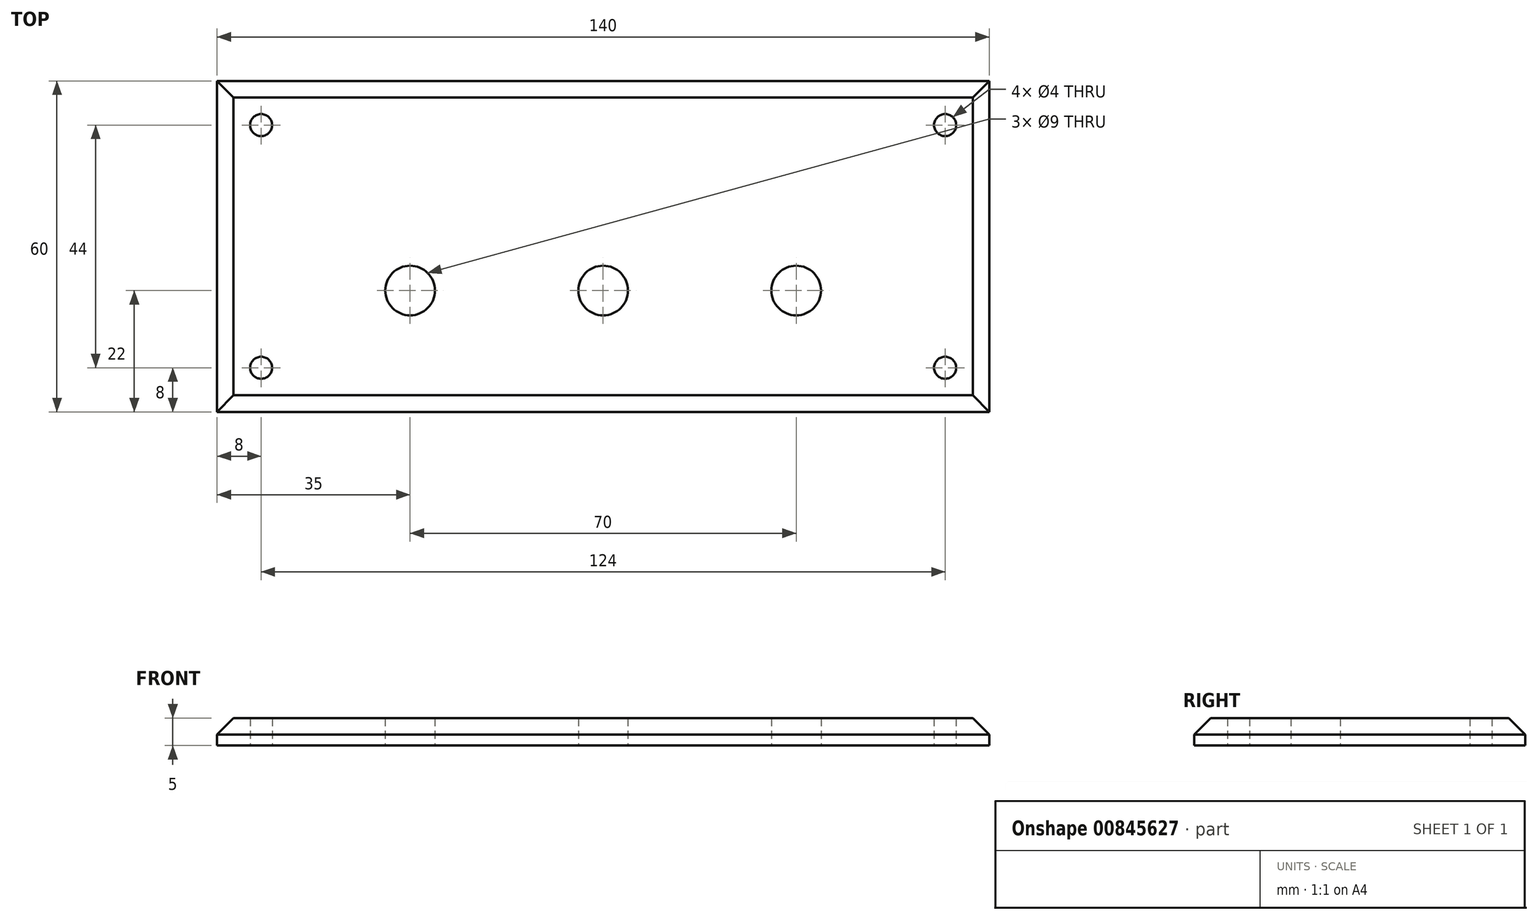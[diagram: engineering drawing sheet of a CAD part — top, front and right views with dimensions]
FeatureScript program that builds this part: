
annotation { "Feature Type Name" : "Feature", "Feature Type Description" : "" }
export const myFeature = defineFeature(function(context is Context, id is Id, definition is map)
    precondition{}
    {
        {
            var Q0;
            Q0=qCreatedBy(makeId("Top.planeOp"),FACE);
            var sketch = newSketch(context, id + "F0", { "sketchPlane" : qUnion([Q0])});
            skLineSegment(sketch, "E0.bottom", {"start": v(-70, 30) * mm, "end": v(70, 30) * mm});
            skLineSegment(sketch, "E0.top", {"start": v(-70, -30) * mm, "end": v(70, -30) * mm});
            skLineSegment(sketch, "E0.left", {"start": v(-70, 30) * mm, "end": v(-70, -30) * mm});
            skLineSegment(sketch, "E0.right", {"start": v(70, 30) * mm, "end": v(70, -30) * mm});
            skCircle(sketch, "E1", {"center": v(-62, 22) * mm, "radius": 2 * mm});
            skCircle(sketch, "E2.MirrorC", {"center": v(62, 22) * mm, "radius": 2 * mm});
            skCircle(sketch, "E3.MirrorC", {"center": v(-62, -22) * mm, "radius": 2 * mm});
            skCircle(sketch, "E4.MirrorC", {"center": v(62, -22) * mm, "radius": 2 * mm});
            skCircle(sketch, "E5", {"center": v(-35, -8) * mm, "radius": 4.5 * mm});
            skCircle(sketch, "E6", {"center": v(0, -8) * mm, "radius": 4.5 * mm});
            skCircle(sketch, "E7.MirrorC", {"center": v(35, -8) * mm, "radius": 4.5 * mm});
            skSolve(sketch);
        }
        {
            var Q0;
            Q0=makeQuery(id+"F0.imprint","IMPRINT",FACE,{"disambiguationData":[TD([[makeQuery(id+"F0.imprint","IMPRINT",EDGE,{"derivedFrom":sQuery(id+"F0.wireOp",EDGE,"E0.bottom")}),-1.0]])]});
            extrude(context, id + "F1", {"entities" : qUnion([Q0]), "depth" : 5 * mm, "offsetDistance" : 25 * mm});
        }
        {
            var Q0;
            Q0=makeQuery(id+"F1.opExtrude","CAP_EDGE",EDGE,{"disambiguationData":[OSD([sQuery(id+"F0.wireOp",EDGE,"E0.top")])],"isStart":false});
            var Q1;
            Q1=makeQuery(id+"F1.opExtrude","CAP_EDGE",EDGE,{"disambiguationData":[OSD([sQuery(id+"F0.wireOp",EDGE,"E0.left")])],"isStart":false});
            var Q2;
            Q2=makeQuery(id+"F1.opExtrude","CAP_EDGE",EDGE,{"disambiguationData":[OSD([sQuery(id+"F0.wireOp",EDGE,"E0.bottom")])],"isStart":false});
            var Q3;
            Q3=makeQuery(id+"F1.opExtrude","CAP_EDGE",EDGE,{"disambiguationData":[OSD([sQuery(id+"F0.wireOp",EDGE,"E0.right")])],"isStart":false});
            chamfer(context, id + "F2", {"entities" : qUnion([Q0, Q1, Q2, Q3]), "chamferType" : ChamferType.OFFSET_ANGLE, "width" : 3 * mm, "oppositeDirection" : false, "angle" : 45 * degree, "tangentPropagation" : true});
        }
    });
